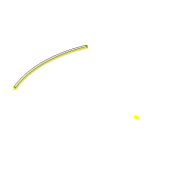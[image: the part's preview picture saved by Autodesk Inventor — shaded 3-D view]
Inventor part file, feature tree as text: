
AUTODESK INVENTOR PART (.ipt)
format: ipt  version: 2022 (Build 260153000, 153)  size: 108,544 bytes
history: native  units: mm
features: sketch x2, extrude x1, fillet x1, projected_geometry x1
ambient origin geometry x8: Origin, YZ Plane, XZ Plane, XY Plane, X Axis, Y Axis, Z Axis, Center Point
bodies: Solid1 (feature_tree)
feature tree (5):
  extrude  "Extrusion1"  Depth=10.0mm
  sketch  "Sketch2"  dims[d3=3.0mm d4=8.0mm d5=0.0mm d12=500.0mm d13=500.0mm d14=2.0mm]
  fillet  "Fillet1"  Radius=3.0mm
  sketch  "Sketch1"  dims[d0=382.775mm d1=10.0mm d2=3.0mm]
  projected_geometry  "Projected Loop1"
